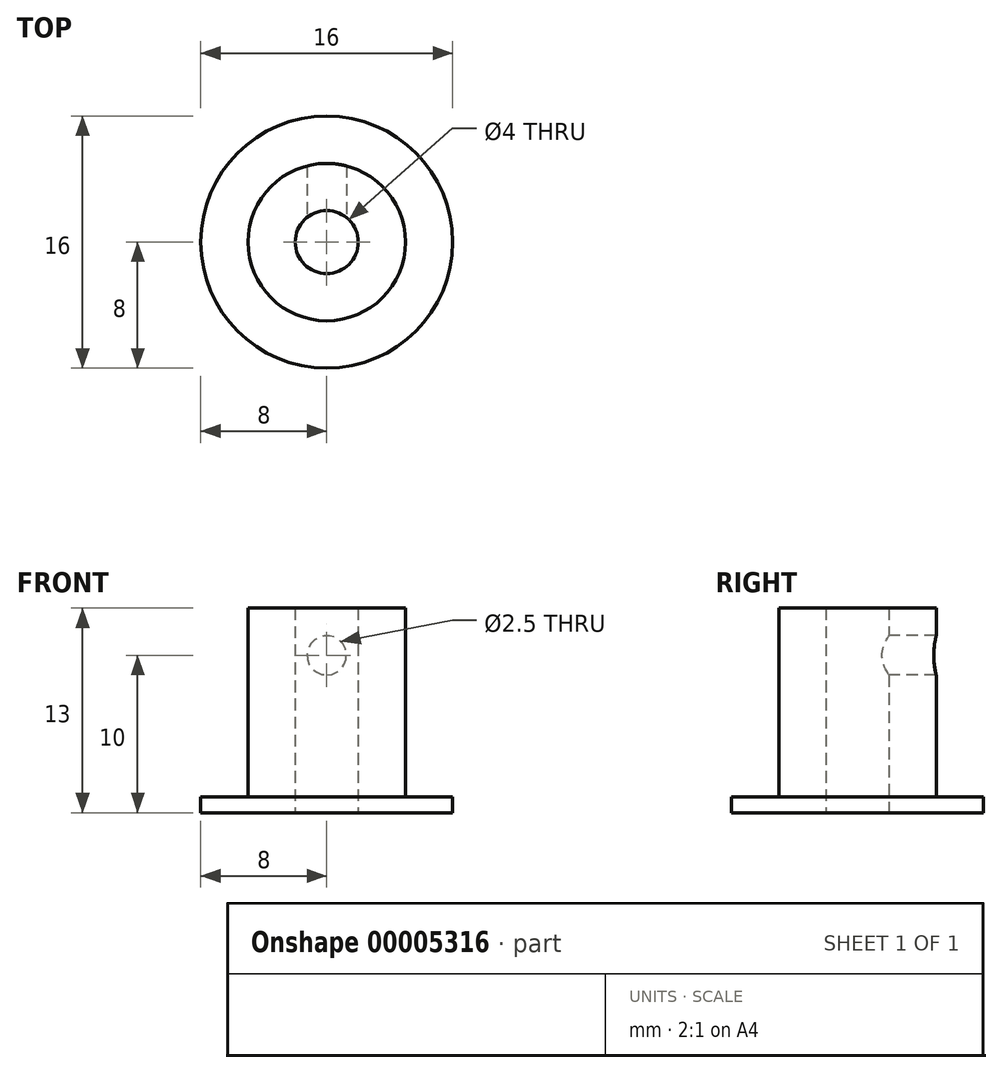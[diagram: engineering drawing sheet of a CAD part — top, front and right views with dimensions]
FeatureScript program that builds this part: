
annotation { "Feature Type Name" : "Feature", "Feature Type Description" : "" }
export const myFeature = defineFeature(function(context is Context, id is Id, definition is map)
    precondition{}
    {
        {
            var Q0;
            Q0=qCreatedBy(makeId("Top.planeOp"),FACE);
            var sketch = newSketch(context, id + "F0", { "sketchPlane" : qUnion([Q0])});
            skCircle(sketch, "E0", {"center": v(0, 0) * mm, "radius": 2 * mm});
            skCircle(sketch, "E1", {"center": v(0, 0) * mm, "radius": 5 * mm});
            skCircle(sketch, "E2", {"center": v(0, 0) * mm, "radius": 8 * mm});
            skSolve(sketch);
        }
        {
            var Q0;
            Q0=makeQuery(id+"F0.imprint","IMPRINT",FACE,{"disambiguationData":[TD([[makeQuery(id+"F0.imprint","IMPRINT",EDGE,{"derivedFrom":sQuery(id+"F0.wireOp",EDGE,"E0")}),-1.0]])]});
            extrude(context, id + "F1", {"entities" : qUnion([Q0]), "depth" : 12 * mm});
        }
        {
            var Q0;
            Q0=makeQuery(id+"F0.imprint","IMPRINT",FACE,{"disambiguationData":[TD([[makeQuery(id+"F0.imprint","IMPRINT",EDGE,{"derivedFrom":sQuery(id+"F0.wireOp",EDGE,"E0")}),-1.0]])]});
            var Q1;
            Q1=makeQuery(id+"F0.imprint","IMPRINT",FACE,{"disambiguationData":[TD([[makeQuery(id+"F0.imprint","IMPRINT",EDGE,{"derivedFrom":sQuery(id+"F0.wireOp",EDGE,"E1")}),-1.0]])]});
            extrude(context, id + "F2", {"entities" : qUnion([Q0, Q1]), "operationType" : NewBodyOperationType.ADD, "oppositeDirection" : true, "depth" : 1 * mm});
        }
        {
            var Q0;
            Q0=qCreatedBy(makeId("Front.planeOp"),FACE);
            var sketch = newSketch(context, id + "F3", { "sketchPlane" : qUnion([Q0])});
            skLineSegment(sketch, "E3.0", {"start": v(-5, 12) * mm, "end": v(5, 12) * mm});
            skCircle(sketch, "E4", {"center": v(0, 9) * mm, "radius": 1.25 * mm});
            skSolve(sketch);
        }
        {
            var Q0;
            Q0=makeQuery(id+"F3.imprint","IMPRINT",FACE,{"disambiguationData":[TD([[makeQuery(id+"F3.imprint","IMPRINT",EDGE,{"derivedFrom":sQuery(id+"F3.wireOp",EDGE,"E4")}),1.0]])]});
            var Q1;
            Q1=sQuery(id+"F3.wireOp",EDGE,"E4");
            var Q2;
            Q2=makeQuery(id+"F1.opExtrude","SWEPT_FACE",FACE,{"disambiguationData":[OSD([sQuery(id+"F0.wireOp",EDGE,"E1")])]});
            extrude(context, id + "F4", {"entities" : qUnion([Q0]), "operationType" : NewBodyOperationType.REMOVE, "surfaceEntities" : qUnion([Q1]), "endBound" : BoundingType.UP_TO_SURFACE, "oppositeDirection" : true, "endBoundEntityFace" : qUnion([Q2]), "depth" : 25 * mm});
        }
    });
